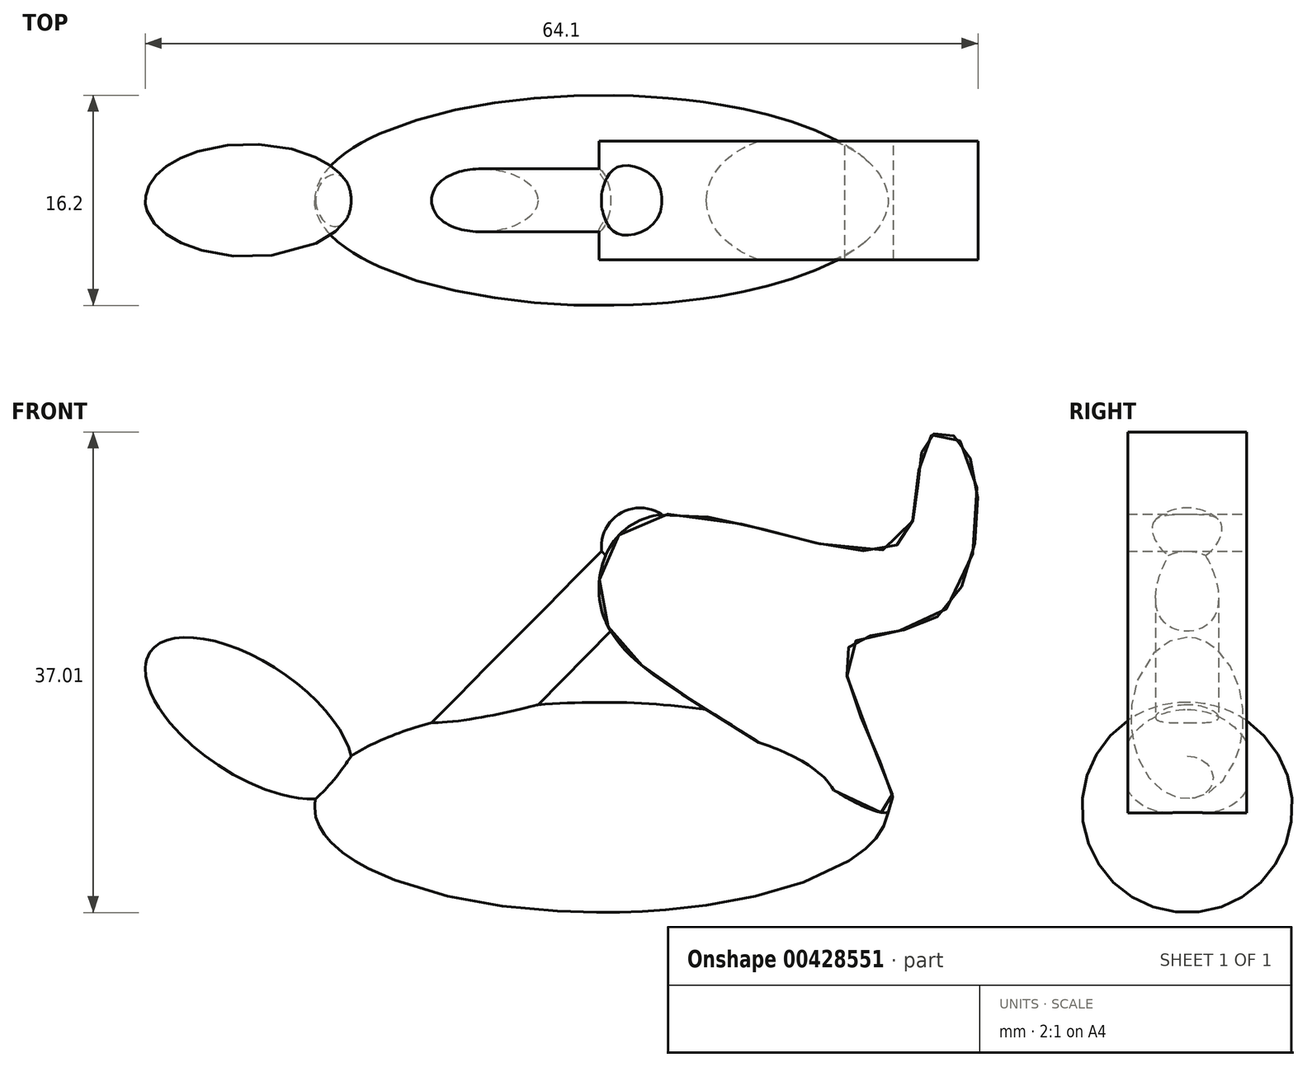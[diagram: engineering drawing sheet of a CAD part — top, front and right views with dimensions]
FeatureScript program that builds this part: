
annotation { "Feature Type Name" : "Feature", "Feature Type Description" : "" }
export const myFeature = defineFeature(function(context is Context, id is Id, definition is map)
    precondition{}
    {
        {
            var Q0;
            Q0=qCreatedBy(makeId("Front.planeOp"),FACE);
            var sketch = newSketch(context, id + "F0", { "sketchPlane" : qUnion([Q0])});
            skEllipse(sketch, "E0", {"center": v(0, 0) * mm, "majorRadius": 22.08 * mm, "minorRadius": 8.1 * mm, "majorAxis": v(1, 0)});
            skLineSegment(sketch, "E1", {"start": v(-22.08, 0) * mm, "end": v(22.08, 0) * mm});
            skSolve(sketch);
        }
        {
            var Q0;
            {var subQ0=sQuery(id+"F0.wireOp",EDGE,"E1");Q0=makeQuery(id+"F0.imprint","IMPRINT",FACE,{"disambiguationData":[TD([[makeQuery(id+"F0.imprint","IMPRINT",EDGE,{"derivedFrom":subQ0}),1.0]])]});}
            var Q1;
            Q1=sQuery(id+"F0.wireOp",EDGE,"E1");
            revolve(context, id + "F1", {"entities" : qUnion([Q0]), "axis" : qUnion([Q1]), "revolveType" : RevolveType.FULL});
        }
        {
            var Q0;
            Q0=qCreatedBy(makeId("Front.planeOp"),FACE);
            var sketch = newSketch(context, id + "F2", { "sketchPlane" : qUnion([Q0])});
            skEllipse(sketch, "E2", {"center": v(-27.15, 6.88) * mm, "majorRadius": 9.14 * mm, "minorRadius": 4.33 * mm, "majorAxis": v(0.83, -0.55)});
            skLineSegment(sketch, "E3", {"start": v(-34.76, 11.95) * mm, "end": v(-19.55, 1.81) * mm});
            skSolve(sketch);
        }
        {
            var Q0;
            {var subQ0=sQuery(id+"F2.wireOp",EDGE,"E3");Q0=makeQuery(id+"F2.imprint","IMPRINT",FACE,{"disambiguationData":[TD([[makeQuery(id+"F2.imprint","IMPRINT",EDGE,{"derivedFrom":subQ0}),1.0]])]});}
            var Q1;
            Q1=sQuery(id+"F2.wireOp",EDGE,"E3");
            revolve(context, id + "F3", {"operationType" : NewBodyOperationType.ADD, "entities" : qUnion([Q0]), "axis" : qUnion([Q1]), "revolveType" : RevolveType.FULL});
        }
        {
            var Q0;
            Q0=qCreatedBy(makeId("Front.planeOp"),FACE);
            var sketch = newSketch(context, id + "F4", { "sketchPlane" : qUnion([Q0])});
            skFitSpline(sketch, "E4", {"points": [v(10.86, 5.8) * mm, v(0, 15.2) * mm, v(3.98, 22.45) * mm, v(22.8, 20.27) * mm, v(24.98, 28.24) * mm, v(27.88, 27.88) * mm, v(26.07, 14.84) * mm, v(18.83, 11.95) * mm, v(22.45, 0) * mm, v(10.86, 5.8) * mm]});
            skSolve(sketch);
        }
        {
            var Q0;
            Q0 = qSketchRegion(id + "F4", true);
            extrude(context, id + "F5", {"entities" : qUnion([Q0]), "operationType" : NewBodyOperationType.ADD, "depth" : 4.57 * mm});
        }
        {
            var Q0;
            Q0 = qSketchRegion(id + "F4", true);
            extrude(context, id + "F6", {"entities" : qUnion([Q0]), "operationType" : NewBodyOperationType.ADD, "oppositeDirection" : true, "depth" : 4.57 * mm});
        }
        {
            var Q0;
            Q0=qCreatedBy(makeId("Front.planeOp"),FACE);
            var sketch = newSketch(context, id + "F7", { "sketchPlane" : qUnion([Q0])});
            skLineSegment(sketch, "E5", {"start": v(-12.72, 0) * mm, "end": v(5.09, 17.98) * mm});
            skLineSegment(sketch, "E6", {"start": v(-19.55, 0) * mm, "end": v(0, 19.74) * mm});
            skLineSegment(sketch, "E7", {"start": v(-12.72, 0) * mm, "end": v(-19.55, 0) * mm});
            skLineSegment(sketch, "E8", {"start": v(0, 19.74) * mm, "end": v(5.09, 17.98) * mm});
            skLineSegment(sketch, "E9", {"start": v(-16.14, 0) * mm, "end": v(11.9, 28.3) * mm});
            skArc(sketch, "E10", {"start": v(5.09, 17.98) * mm, "mid": v(3.94, 22.9) * mm, "end": v(0, 19.74) * mm});
            skSolve(sketch);
        }
        {
            var Q0;
            {var subQ0=sQuery(id+"F7.wireOp",EDGE,"E6");Q0=makeQuery(id+"F7.imprint","IMPRINT",FACE,{"disambiguationData":[TD([[makeQuery(id+"F7.imprint","IMPRINT",EDGE,{"derivedFrom":subQ0}),-1.0]])]});}
            var Q1;
            {var subQ0=sQuery(id+"F7.wireOp",EDGE,"E10");var subQ3=sQuery(id+"F7.wireOp",EDGE,"E9");var subQ5=makeQuery(id+"F7.imprint","INTERSECT",VERTEX,{"derivedFrom":[subQ3,subQ0]});Q1=makeQuery(id+"F7.imprint","IMPRINT",FACE,{"disambiguationData":[TD([[makeQuery(id+"F7.imprint","IMPRINT",EDGE,{"disambiguationData":[TD([[subQ5,1.0]])],"derivedFrom":subQ3}),1.0]])]});}
            var Q2;
            Q2=sQuery(id+"F7.wireOp",EDGE,"E9");
            revolve(context, id + "F8", {"operationType" : NewBodyOperationType.ADD, "entities" : qUnion([Q0, Q1]), "axis" : qUnion([Q2]), "revolveType" : RevolveType.FULL});
        }
    });
